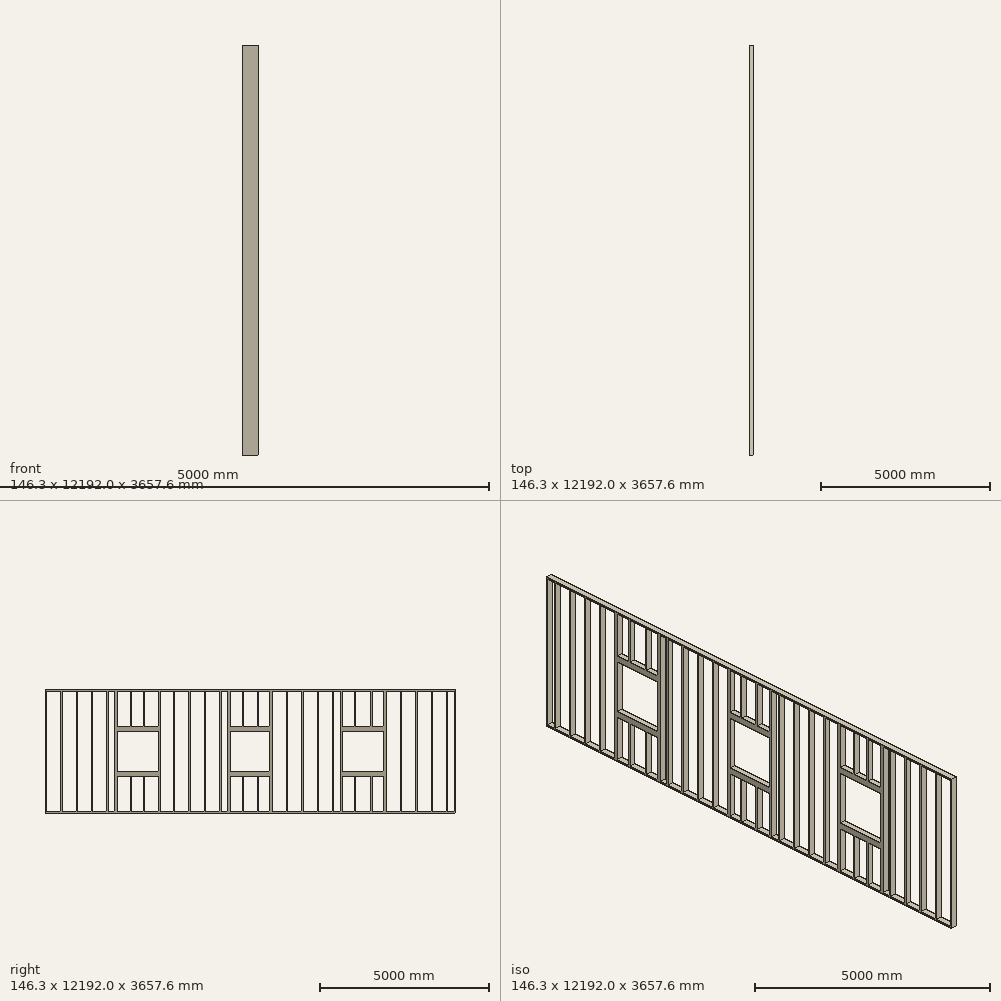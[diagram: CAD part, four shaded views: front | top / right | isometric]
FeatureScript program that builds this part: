
annotation { "Feature Type Name" : "Feature", "Feature Type Description" : "" }
export const myFeature = defineFeature(function(context is Context, id is Id, definition is map)
    precondition{}
    {
        {
            var Q0;
            Q0=qCreatedBy(makeId("Right.planeOp"),FACE);
            var sketch = newSketch(context, id + "F0", { "sketchPlane" : qUnion([Q0])});
            skLineSegment(sketch, "E0.bottom", {"start": v(0, 0) * mm, "end": v(12192, 0) * mm});
            skLineSegment(sketch, "E0.top", {"start": v(0, 3657.6) * mm, "end": v(12192, 3657.6) * mm});
            skLineSegment(sketch, "E0.left", {"start": v(0, 0) * mm, "end": v(0, 3657.6) * mm});
            skLineSegment(sketch, "E0.right", {"start": v(12192, 0) * mm, "end": v(12192, 3657.6) * mm});
            skLineSegment(sketch, "E1.0", {"start": v(38.1, 38.1) * mm, "end": v(38.1, 3619.5) * mm});
            skLineSegment(sketch, "E1.1", {"start": v(38.1, 38.1) * mm, "end": v(457.2, 38.1) * mm});
            skLineSegment(sketch, "E1.2", {"start": v(12153.9, 38.1) * mm, "end": v(12153.9, 3619.5) * mm});
            skLineSegment(sketch, "E1.3", {"start": v(38.1, 3619.5) * mm, "end": v(457.2, 3619.5) * mm});
            skLineSegment(sketch, "E2", {"start": v(457.2, 3619.5) * mm, "end": v(457.2, 38.1) * mm});
            skLineSegment(sketch, "E3", {"start": v(495.3, 3619.5) * mm, "end": v(495.3, 38.1) * mm});
            skLineSegment(sketch, "E4.trimOffspring", {"start": v(495.3, 3619.5) * mm, "end": v(914.4, 3619.5) * mm});
            skLineSegment(sketch, "E5.trimOffspring", {"start": v(495.3, 38.1) * mm, "end": v(914.4, 38.1) * mm});
            skLineSegment(sketch, "E6.1.0.0", {"start": v(914.4, 3619.5) * mm, "end": v(914.4, 38.1) * mm});
            skLineSegment(sketch, "E6.1.0.1", {"start": v(952.5, 3619.5) * mm, "end": v(952.5, 38.1) * mm});
            skLineSegment(sketch, "E6.2.0.0", {"start": v(1371.6, 3619.5) * mm, "end": v(1371.6, 38.1) * mm});
            skLineSegment(sketch, "E6.2.0.1", {"start": v(1409.7, 3619.5) * mm, "end": v(1409.7, 38.1) * mm});
            skLineSegment(sketch, "E6.3.0.0", {"start": v(1828.8, 3619.5) * mm, "end": v(1828.8, 38.1) * mm});
            skLineSegment(sketch, "E6.3.0.1", {"start": v(1866.9, 3619.5) * mm, "end": v(1866.9, 38.1) * mm});
            skLineSegment(sketch, "E6.4.0.0", {"start": v(2057.4, 3619.5) * mm, "end": v(2057.4, 38.1) * mm});
            skLineSegment(sketch, "E6.5.0.0", {"start": v(2514.6, 3619.5) * mm, "end": v(2514.6, 2584.7) * mm});
            skLineSegment(sketch, "E6.5.0.1", {"start": v(2552.7, 3619.5) * mm, "end": v(2552.7, 2584.7) * mm});
            skLineSegment(sketch, "E6.6.0.1", {"start": v(3352.8, 2438.4) * mm, "end": v(3352.8, 1219.2) * mm});
            skLineSegment(sketch, "E6.8.0.0", {"start": v(4267.2, 3619.5) * mm, "end": v(4267.2, 38.1) * mm});
            skLineSegment(sketch, "E6.8.0.1", {"start": v(4305.3, 3619.5) * mm, "end": v(4305.3, 38.1) * mm});
            skLineSegment(sketch, "E6.9.0.0", {"start": v(4724.4, 3619.5) * mm, "end": v(4724.4, 38.1) * mm});
            skLineSegment(sketch, "E6.9.0.1", {"start": v(4762.5, 3619.5) * mm, "end": v(4762.5, 38.1) * mm});
            skLineSegment(sketch, "E6.10.0.0", {"start": v(5181.6, 3619.5) * mm, "end": v(5181.6, 38.1) * mm});
            skLineSegment(sketch, "E6.10.0.1", {"start": v(5219.7, 3619.5) * mm, "end": v(5219.7, 38.1) * mm});
            skLineSegment(sketch, "E6.11.0.0", {"start": v(5410.2, 3619.5) * mm, "end": v(5410.2, 38.1) * mm});
            skLineSegment(sketch, "E6.11.0.1", {"start": v(5486.4, 3619.5) * mm, "end": v(5486.4, 2584.7) * mm});
            skLineSegment(sketch, "E6.12.0.0", {"start": v(5852.16, 3619.5) * mm, "end": v(5852.16, 2584.7) * mm});
            skLineSegment(sketch, "E6.12.0.1", {"start": v(5890.26, 3619.5) * mm, "end": v(5890.26, 2584.7) * mm});
            skLineSegment(sketch, "E6.13.0.0", {"start": v(6309.36, 3619.5) * mm, "end": v(6309.36, 2584.7) * mm});
            skLineSegment(sketch, "E6.13.0.1", {"start": v(6347.46, 3619.5) * mm, "end": v(6347.46, 2584.7) * mm});
            skLineSegment(sketch, "E6.14.0.0", {"start": v(6667.5, 3619.5) * mm, "end": v(6667.5, 2584.7) * mm});
            skLineSegment(sketch, "E6.14.0.1", {"start": v(6743.7, 3619.5) * mm, "end": v(6743.7, 38.1) * mm});
            skLineSegment(sketch, "E6.15.0.0", {"start": v(7162.8, 3619.5) * mm, "end": v(7162.8, 38.1) * mm});
            skLineSegment(sketch, "E6.15.0.1", {"start": v(7200.9, 3619.5) * mm, "end": v(7200.9, 38.1) * mm});
            skLineSegment(sketch, "E6.16.0.0", {"start": v(7620, 3619.5) * mm, "end": v(7620, 38.1) * mm});
            skLineSegment(sketch, "E6.16.0.1", {"start": v(7658.1, 3619.5) * mm, "end": v(7658.1, 38.1) * mm});
            skLineSegment(sketch, "E6.17.0.0", {"start": v(8077.2, 3619.5) * mm, "end": v(8077.2, 38.1) * mm});
            skLineSegment(sketch, "E6.17.0.1", {"start": v(8115.3, 3619.5) * mm, "end": v(8115.3, 38.1) * mm});
            skLineSegment(sketch, "E6.18.0.0", {"start": v(8763, 3619.5) * mm, "end": v(8763, 38.1) * mm});
            skLineSegment(sketch, "E6.18.0.1", {"start": v(8839.2, 3619.5) * mm, "end": v(8839.2, 2584.7) * mm});
            skLineSegment(sketch, "E6.19.0.0", {"start": v(9182.1, 3619.5) * mm, "end": v(9182.1, 2584.7) * mm});
            skLineSegment(sketch, "E6.19.0.1", {"start": v(9220.2, 3619.5) * mm, "end": v(9220.2, 2584.7) * mm});
            skLineSegment(sketch, "E6.20.0.0", {"start": v(9677.4, 3619.5) * mm, "end": v(9677.4, 2584.7) * mm});
            skLineSegment(sketch, "E6.20.0.1", {"start": v(9715.5, 3619.5) * mm, "end": v(9715.5, 2584.7) * mm});
            skLineSegment(sketch, "E6.21.0.0", {"start": v(10058.4, 3619.5) * mm, "end": v(10058.4, 2584.7) * mm});
            skLineSegment(sketch, "E6.21.0.1", {"start": v(10134.6, 3619.5) * mm, "end": v(10134.6, 38.1) * mm});
            skLineSegment(sketch, "E6.22.0.0", {"start": v(10553.7, 3619.5) * mm, "end": v(10553.7, 38.1) * mm});
            skLineSegment(sketch, "E6.22.0.1", {"start": v(10591.8, 3619.5) * mm, "end": v(10591.8, 38.1) * mm});
            skLineSegment(sketch, "E6.23.0.0", {"start": v(11010.9, 3619.5) * mm, "end": v(11010.9, 38.1) * mm});
            skLineSegment(sketch, "E6.23.0.1", {"start": v(11049, 3619.5) * mm, "end": v(11049, 38.1) * mm});
            skLineSegment(sketch, "E6.24.0.0", {"start": v(11468.1, 3619.5) * mm, "end": v(11468.1, 38.1) * mm});
            skLineSegment(sketch, "E6.24.0.1", {"start": v(11506.2, 3619.5) * mm, "end": v(11506.2, 38.1) * mm});
            skLineSegment(sketch, "E6.25.0.0", {"start": v(11925.3, 3619.5) * mm, "end": v(11925.3, 38.1) * mm});
            skLineSegment(sketch, "E6.25.0.1", {"start": v(11963.4, 3619.5) * mm, "end": v(11963.4, 38.1) * mm});
            skLineSegment(sketch, "E6.direction1", {"start": v(495.3, 38.1) * mm, "end": v(914.4, 38.1) * mm, "construction": true});
            skLineSegment(sketch, "E7.trimOffspring", {"start": v(952.5, 3619.5) * mm, "end": v(1371.6, 3619.5) * mm});
            skLineSegment(sketch, "E8.trimOffspring", {"start": v(1409.7, 3619.5) * mm, "end": v(1828.8, 3619.5) * mm});
            skLineSegment(sketch, "E9.trimOffspring", {"start": v(1866.9, 3619.5) * mm, "end": v(2057.4, 3619.5) * mm});
            skLineSegment(sketch, "E10.trimOffspring", {"start": v(2133.6, 3619.5) * mm, "end": v(2514.6, 3619.5) * mm});
            skLineSegment(sketch, "E11.trimOffspring", {"start": v(2552.7, 3619.5) * mm, "end": v(2914.65, 3619.5) * mm});
            skLineSegment(sketch, "E12.trimOffspring", {"start": v(3429, 3619.5) * mm, "end": v(3810, 3619.5) * mm});
            skLineSegment(sketch, "E13.trimOffspring", {"start": v(3848.1, 3619.5) * mm, "end": v(4267.2, 3619.5) * mm});
            skLineSegment(sketch, "E14.trimOffspring", {"start": v(4305.3, 3619.5) * mm, "end": v(4724.4, 3619.5) * mm});
            skLineSegment(sketch, "E15.trimOffspring", {"start": v(4762.5, 3619.5) * mm, "end": v(5181.6, 3619.5) * mm});
            skLineSegment(sketch, "E16.trimOffspring", {"start": v(5219.7, 3619.5) * mm, "end": v(5410.2, 3619.5) * mm});
            skLineSegment(sketch, "E17.trimOffspring", {"start": v(5486.4, 3619.5) * mm, "end": v(5852.16, 3619.5) * mm});
            skLineSegment(sketch, "E18.trimOffspring", {"start": v(5890.26, 3619.5) * mm, "end": v(6309.36, 3619.5) * mm});
            skLineSegment(sketch, "E19.trimOffspring", {"start": v(6347.46, 3619.5) * mm, "end": v(6667.5, 3619.5) * mm});
            skLineSegment(sketch, "E20.trimOffspring", {"start": v(6743.7, 3619.5) * mm, "end": v(7162.8, 3619.5) * mm});
            skLineSegment(sketch, "E21.trimOffspring", {"start": v(7200.9, 3619.5) * mm, "end": v(7620, 3619.5) * mm});
            skLineSegment(sketch, "E22.trimOffspring", {"start": v(7658.1, 3619.5) * mm, "end": v(8077.2, 3619.5) * mm});
            skLineSegment(sketch, "E23.trimOffspring", {"start": v(8115.3, 3619.5) * mm, "end": v(8763, 3619.5) * mm});
            skLineSegment(sketch, "E24.trimOffspring", {"start": v(8839.2, 3619.5) * mm, "end": v(9182.1, 3619.5) * mm});
            skLineSegment(sketch, "E25.trimOffspring", {"start": v(9220.2, 3619.5) * mm, "end": v(9677.4, 3619.5) * mm});
            skLineSegment(sketch, "E26.trimOffspring", {"start": v(9715.5, 3619.5) * mm, "end": v(10058.4, 3619.5) * mm});
            skLineSegment(sketch, "E27.trimOffspring", {"start": v(10134.6, 3619.5) * mm, "end": v(10553.7, 3619.5) * mm});
            skLineSegment(sketch, "E28.trimOffspring", {"start": v(10591.8, 3619.5) * mm, "end": v(11010.9, 3619.5) * mm});
            skLineSegment(sketch, "E29.trimOffspring", {"start": v(11049, 3619.5) * mm, "end": v(11468.1, 3619.5) * mm});
            skLineSegment(sketch, "E30.trimOffspring", {"start": v(11506.2, 3619.5) * mm, "end": v(11925.3, 3619.5) * mm});
            skLineSegment(sketch, "E31.trimOffspring", {"start": v(11963.4, 3619.5) * mm, "end": v(12153.9, 3619.5) * mm});
            skLineSegment(sketch, "E32.trimOffspring", {"start": v(11963.4, 38.1) * mm, "end": v(12153.9, 38.1) * mm});
            skLineSegment(sketch, "E33.trimOffspring", {"start": v(11506.2, 38.1) * mm, "end": v(11925.3, 38.1) * mm});
            skLineSegment(sketch, "E34.trimOffspring", {"start": v(11049, 38.1) * mm, "end": v(11468.1, 38.1) * mm});
            skLineSegment(sketch, "E35.trimOffspring", {"start": v(10591.8, 38.1) * mm, "end": v(11010.9, 38.1) * mm});
            skLineSegment(sketch, "E36.trimOffspring", {"start": v(10134.6, 38.1) * mm, "end": v(10553.7, 38.1) * mm});
            skLineSegment(sketch, "E37.trimOffspring", {"start": v(9715.5, 38.1) * mm, "end": v(10058.4, 38.1) * mm});
            skLineSegment(sketch, "E38.trimOffspring", {"start": v(9220.2, 38.1) * mm, "end": v(9677.4, 38.1) * mm});
            skLineSegment(sketch, "E39.trimOffspring", {"start": v(8839.2, 38.1) * mm, "end": v(9182.1, 38.1) * mm});
            skLineSegment(sketch, "E40.trimOffspring", {"start": v(8115.3, 38.1) * mm, "end": v(8534.4, 38.1) * mm});
            skLineSegment(sketch, "E41.trimOffspring", {"start": v(7658.1, 38.1) * mm, "end": v(8077.2, 38.1) * mm});
            skLineSegment(sketch, "E42.trimOffspring", {"start": v(7200.9, 38.1) * mm, "end": v(7620, 38.1) * mm});
            skLineSegment(sketch, "E43.trimOffspring", {"start": v(6743.7, 38.1) * mm, "end": v(7162.8, 38.1) * mm});
            skLineSegment(sketch, "E44.trimOffspring", {"start": v(6347.46, 38.1) * mm, "end": v(6667.5, 38.1) * mm});
            skLineSegment(sketch, "E45.trimOffspring", {"start": v(5890.26, 38.1) * mm, "end": v(6309.36, 38.1) * mm});
            skLineSegment(sketch, "E46.trimOffspring", {"start": v(5486.4, 38.1) * mm, "end": v(5852.16, 38.1) * mm});
            skLineSegment(sketch, "E47.trimOffspring", {"start": v(5219.7, 38.1) * mm, "end": v(5410.2, 38.1) * mm});
            skLineSegment(sketch, "E48.trimOffspring", {"start": v(4762.5, 38.1) * mm, "end": v(5181.6, 38.1) * mm});
            skLineSegment(sketch, "E49.trimOffspring", {"start": v(4305.3, 38.1) * mm, "end": v(4724.4, 38.1) * mm});
            skLineSegment(sketch, "E50.trimOffspring", {"start": v(3848.1, 38.1) * mm, "end": v(4267.2, 38.1) * mm});
            skLineSegment(sketch, "E51.trimOffspring", {"start": v(3429, 38.1) * mm, "end": v(3810, 38.1) * mm});
            skLineSegment(sketch, "E52.trimOffspring", {"start": v(2552.7, 38.1) * mm, "end": v(2914.65, 38.1) * mm});
            skLineSegment(sketch, "E53.trimOffspring", {"start": v(2133.6, 38.1) * mm, "end": v(2514.6, 38.1) * mm});
            skLineSegment(sketch, "E54.trimOffspring", {"start": v(1866.9, 38.1) * mm, "end": v(2057.4, 38.1) * mm});
            skLineSegment(sketch, "E55.trimOffspring", {"start": v(1409.7, 38.1) * mm, "end": v(1828.8, 38.1) * mm});
            skLineSegment(sketch, "E56.trimOffspring", {"start": v(952.5, 38.1) * mm, "end": v(1371.6, 38.1) * mm});
            skLineSegment(sketch, "E57.bottom", {"start": v(2133.6, 2438.4) * mm, "end": v(3352.8, 2438.4) * mm});
            skLineSegment(sketch, "E57.top", {"start": v(2133.6, 1219.2) * mm, "end": v(3352.8, 1219.2) * mm});
            skLineSegment(sketch, "E57.left", {"start": v(2133.6, 2438.4) * mm, "end": v(2133.6, 1219.2) * mm});
            skLineSegment(sketch, "E58", {"start": v(2133.6, 2584.7) * mm, "end": v(2514.6, 2584.7) * mm});
            skLineSegment(sketch, "E59", {"start": v(2133.6, 1072.9) * mm, "end": v(2514.6, 1072.9) * mm});
            skLineSegment(sketch, "E60.trimOffspring", {"start": v(2552.7, 1072.9) * mm, "end": v(2552.7, 38.1) * mm});
            skLineSegment(sketch, "E61.trimOffspring", {"start": v(2514.6, 1072.9) * mm, "end": v(2514.6, 38.1) * mm});
            skLineSegment(sketch, "E62", {"start": v(2133.6, 2584.7) * mm, "end": v(2133.6, 3619.5) * mm});
            skLineSegment(sketch, "E63", {"start": v(3352.8, 3619.5) * mm, "end": v(3352.8, 2584.7) * mm});
            skLineSegment(sketch, "E64", {"start": v(2133.6, 1072.9) * mm, "end": v(2133.6, 38.1) * mm});
            skLineSegment(sketch, "E65", {"start": v(3352.8, 1072.9) * mm, "end": v(3352.8, 38.1) * mm});
            skLineSegment(sketch, "E66.trimOffspring", {"start": v(2552.7, 2584.7) * mm, "end": v(2914.65, 2584.7) * mm});
            skLineSegment(sketch, "E67.trimOffspring", {"start": v(2552.7, 1072.9) * mm, "end": v(2914.65, 1072.9) * mm});
            skLineSegment(sketch, "E68", {"start": v(3429, 38.1) * mm, "end": v(3429, 3619.5) * mm});
            skLineSegment(sketch, "E69.bottom", {"start": v(5486.4, 2438.4) * mm, "end": v(5852.16, 2438.4) * mm});
            skLineSegment(sketch, "E69.top", {"start": v(5486.4, 1219.2) * mm, "end": v(6347.46, 1219.2) * mm});
            skLineSegment(sketch, "E69.left", {"start": v(5486.4, 2438.4) * mm, "end": v(5486.4, 1219.2) * mm});
            skLineSegment(sketch, "E69.right", {"start": v(6667.5, 2438.4) * mm, "end": v(6667.5, 1219.2) * mm});
            skLineSegment(sketch, "E70.trimOffspring", {"start": v(5486.4, 1072.9) * mm, "end": v(5486.4, 38.1) * mm});
            skLineSegment(sketch, "E71.trimOffspring", {"start": v(6667.5, 1072.9) * mm, "end": v(6667.5, 38.1) * mm});
            skLineSegment(sketch, "E72", {"start": v(5486.4, 1072.9) * mm, "end": v(5852.16, 1072.9) * mm});
            skLineSegment(sketch, "E73", {"start": v(5486.4, 2584.7) * mm, "end": v(5852.16, 2584.7) * mm});
            skLineSegment(sketch, "E74.trimOffspring", {"start": v(5852.16, 1072.9) * mm, "end": v(5852.16, 38.1) * mm});
            skLineSegment(sketch, "E75.trimOffspring", {"start": v(5890.26, 1072.9) * mm, "end": v(5890.26, 38.1) * mm});
            skLineSegment(sketch, "E76.trimOffspring", {"start": v(6309.36, 1072.9) * mm, "end": v(6309.36, 38.1) * mm});
            skLineSegment(sketch, "E77.trimOffspring", {"start": v(6347.46, 1072.9) * mm, "end": v(6347.46, 38.1) * mm});
            skLineSegment(sketch, "E78.trimOffspring", {"start": v(5890.26, 1219.2) * mm, "end": v(6309.36, 1219.2) * mm});
            skLineSegment(sketch, "E79.trimOffspring", {"start": v(5890.26, 1072.9) * mm, "end": v(6309.36, 1072.9) * mm});
            skLineSegment(sketch, "E80.trimOffspring", {"start": v(6347.46, 1219.2) * mm, "end": v(6667.5, 1219.2) * mm});
            skLineSegment(sketch, "E81.trimOffspring", {"start": v(6347.46, 1072.9) * mm, "end": v(6667.5, 1072.9) * mm});
            skLineSegment(sketch, "E82.trimOffspring", {"start": v(5890.26, 2584.7) * mm, "end": v(6309.36, 2584.7) * mm});
            skLineSegment(sketch, "E83.trimOffspring", {"start": v(6347.46, 2584.7) * mm, "end": v(6667.5, 2584.7) * mm});
            skLineSegment(sketch, "E84.trimOffspring", {"start": v(5890.26, 2438.4) * mm, "end": v(6309.36, 2438.4) * mm});
            skLineSegment(sketch, "E85.trimOffspring", {"start": v(6347.46, 2438.4) * mm, "end": v(6667.5, 2438.4) * mm});
            skLineSegment(sketch, "E86", {"start": v(5852.16, 2438.4) * mm, "end": v(5890.26, 2438.4) * mm});
            skLineSegment(sketch, "E87", {"start": v(6309.36, 2438.4) * mm, "end": v(6347.46, 2438.4) * mm});
            skLineSegment(sketch, "E88.bottom", {"start": v(8839.2, 2438.4) * mm, "end": v(10058.4, 2438.4) * mm});
            skLineSegment(sketch, "E88.top", {"start": v(8839.2, 1219.2) * mm, "end": v(10058.4, 1219.2) * mm});
            skLineSegment(sketch, "E88.left", {"start": v(8839.2, 2438.4) * mm, "end": v(8839.2, 1219.2) * mm});
            skLineSegment(sketch, "E88.right", {"start": v(10058.4, 2438.4) * mm, "end": v(10058.4, 1219.2) * mm});
            skLineSegment(sketch, "E89.trimOffspring", {"start": v(8839.2, 1072.9) * mm, "end": v(8839.2, 38.1) * mm});
            skLineSegment(sketch, "E90.trimOffspring", {"start": v(10058.4, 1072.9) * mm, "end": v(10058.4, 38.1) * mm});
            skLineSegment(sketch, "E91", {"start": v(8839.2, 1072.9) * mm, "end": v(9182.1, 1072.9) * mm});
            skLineSegment(sketch, "E92", {"start": v(8839.2, 2584.7) * mm, "end": v(9182.1, 2584.7) * mm});
            skLineSegment(sketch, "E93.trimOffspring", {"start": v(9182.1, 1072.9) * mm, "end": v(9182.1, 38.1) * mm});
            skLineSegment(sketch, "E94.trimOffspring", {"start": v(9220.2, 1072.9) * mm, "end": v(9220.2, 38.1) * mm});
            skLineSegment(sketch, "E95.trimOffspring", {"start": v(9677.4, 1072.9) * mm, "end": v(9677.4, 38.1) * mm});
            skLineSegment(sketch, "E96.trimOffspring", {"start": v(9715.5, 1072.9) * mm, "end": v(9715.5, 38.1) * mm});
            skLineSegment(sketch, "E97.trimOffspring", {"start": v(9220.2, 1072.9) * mm, "end": v(9677.4, 1072.9) * mm});
            skLineSegment(sketch, "E98.trimOffspring", {"start": v(9715.5, 1072.9) * mm, "end": v(10058.4, 1072.9) * mm});
            skLineSegment(sketch, "E99.trimOffspring", {"start": v(9220.2, 2584.7) * mm, "end": v(9677.4, 2584.7) * mm});
            skLineSegment(sketch, "E100.trimOffspring", {"start": v(9715.5, 2584.7) * mm, "end": v(10058.4, 2584.7) * mm});
            skLineSegment(sketch, "E101", {"start": v(3810, 3619.5) * mm, "end": v(3810, 38.1) * mm});
            skLineSegment(sketch, "E102", {"start": v(3848.1, 38.1) * mm, "end": v(3848.1, 3619.5) * mm});
            skLineSegment(sketch, "E103", {"start": v(2914.65, 2584.7) * mm, "end": v(2914.65, 3619.5) * mm});
            skPoint(sketch, "E103.endSnap0", {"position": v(2952.75, 3619.5) * mm});
            skLineSegment(sketch, "E104", {"start": v(2952.75, 3619.5) * mm, "end": v(2952.75, 2584.7) * mm});
            skLineSegment(sketch, "E105", {"start": v(2914.65, 1072.9) * mm, "end": v(2914.65, 38.1) * mm});
            skLineSegment(sketch, "E106", {"start": v(2952.75, 1072.9) * mm, "end": v(2952.75, 38.1) * mm});
            skLineSegment(sketch, "E107.trimOffspring", {"start": v(2952.75, 2584.7) * mm, "end": v(3352.8, 2584.7) * mm});
            skLineSegment(sketch, "E108.trimOffspring", {"start": v(2952.75, 3619.5) * mm, "end": v(3352.8, 3619.5) * mm});
            skLineSegment(sketch, "E109.trimOffspring", {"start": v(2952.75, 1072.9) * mm, "end": v(3352.8, 1072.9) * mm});
            skLineSegment(sketch, "E110.trimOffspring", {"start": v(2952.75, 38.1) * mm, "end": v(3352.8, 38.1) * mm});
            skLineSegment(sketch, "E111", {"start": v(8534.4, 3619.5) * mm, "end": v(8534.4, 38.1) * mm});
            skLineSegment(sketch, "E112", {"start": v(8572.5, 3619.5) * mm, "end": v(8572.5, 38.1) * mm});
            skLineSegment(sketch, "E113.trimOffspring", {"start": v(8572.5, 38.1) * mm, "end": v(8763, 38.1) * mm});
            skSolve(sketch);
        }
        {
            var Q0;
            Q0=qSketchRegion(id+"F0",true);
            extrude(context, id + "F1", {"entities" : qUnion([Q0]), "depth" : 146.3 * mm, "offsetDistance" : 30.48 * mm});
        }
    });
